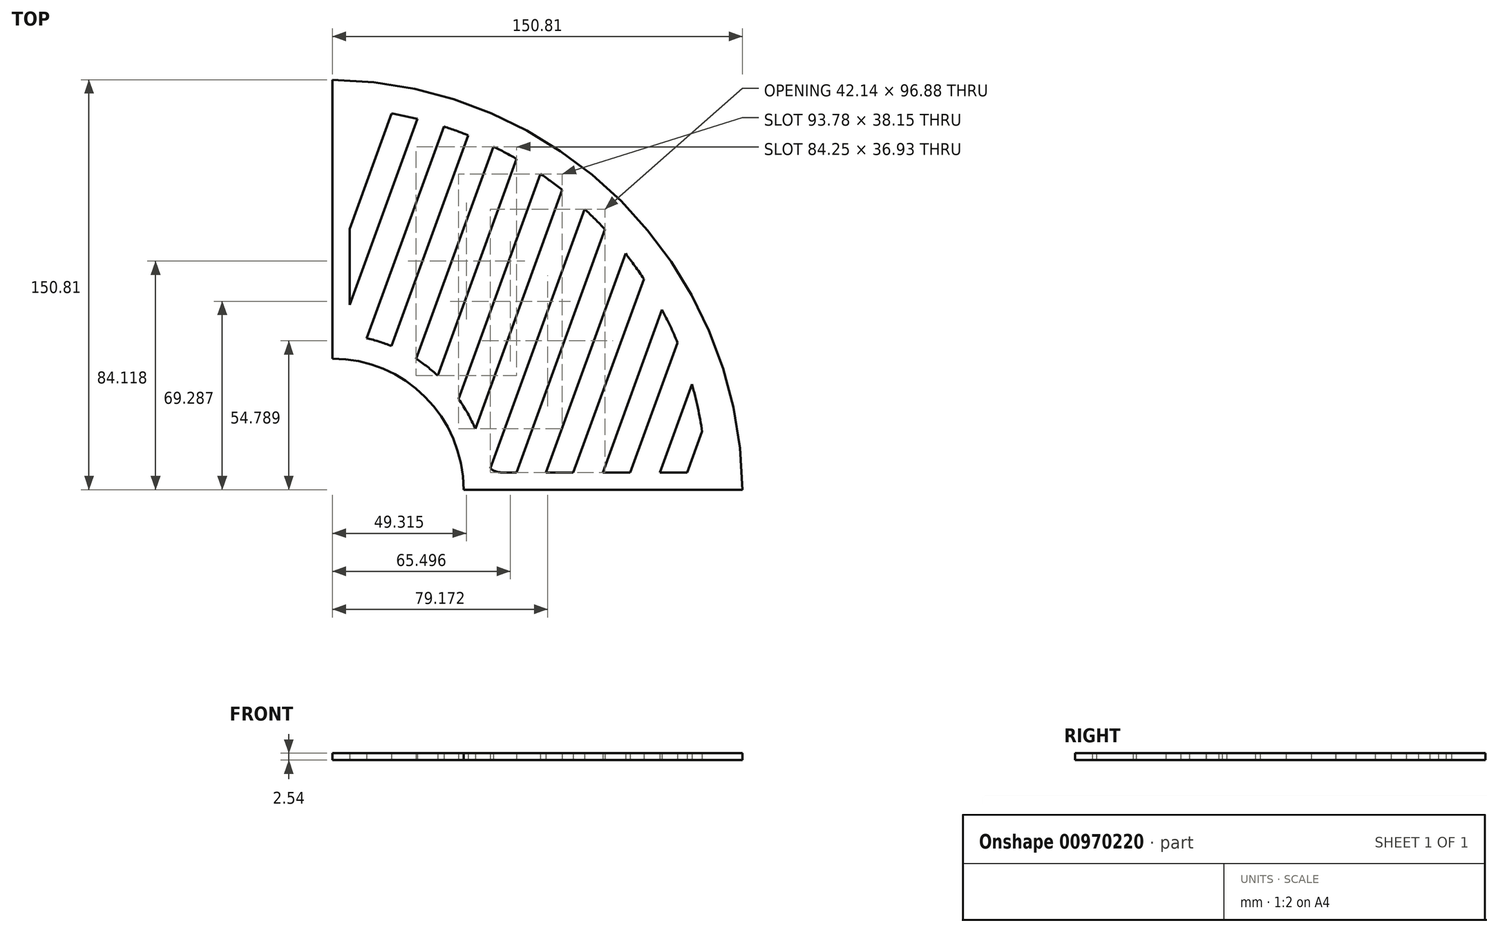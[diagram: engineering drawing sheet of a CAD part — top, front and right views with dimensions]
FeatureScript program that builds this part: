
annotation { "Feature Type Name" : "Feature", "Feature Type Description" : "" }
export const myFeature = defineFeature(function(context is Context, id is Id, definition is map)
    precondition{}
    {
        {
            var Q0;
            Q0=qCreatedBy(makeId("Top.planeOp"),FACE);
            var sketch = newSketch(context, id + "F0", { "sketchPlane" : qUnion([Q0])});
            skLineSegment(sketch, "E0", {"start": v(6.35, 68.05) * mm, "end": v(6.35, 95.9) * mm});
            skLineSegment(sketch, "E1", {"start": v(62.22, 6.35) * mm, "end": v(67.69, 6.35) * mm});
            skArc(sketch, "E2", {"start": v(52.58, 22.4) * mm, "mid": v(49.8, 28.03) * mm, "end": v(46.42, 33.33) * mm});
            skArc(sketch, "E3", {"start": v(136, 21.37) * mm, "mid": v(134.4, 30.18) * mm, "end": v(132.23, 38.87) * mm});
            skPoint(sketch, "E4.visualSharp", {"position": v(6.35, 140.23) * mm});
            skPoint(sketch, "E5.visualSharp", {"position": v(137.4, 6.35) * mm});
            skPoint(sketch, "E6.visualSharp", {"position": v(56.8, 6.35) * mm});
            skArc(sketch, "E6.filletArc", {"start": v(58.1, 7.86) * mm, "mid": v(60.02, 6.74) * mm, "end": v(62.22, 6.35) * mm});
            skPoint(sketch, "E7.visualSharp", {"position": v(6.35, 56.8) * mm});
            skPoint(sketch, "E8", {"position": v(6.35, 62.22) * mm});
            skLineSegment(sketch, "E9", {"start": v(0, 0) * mm, "end": v(150.81, 0) * mm});
            skLineSegment(sketch, "E10", {"start": v(0, 0) * mm, "end": v(0, 150.81) * mm});
            skArc(sketch, "E11", {"start": v(150.81, 0) * mm, "mid": v(106.18, 106.18) * mm, "end": v(0, 150.81) * mm});
            skLineSegment(sketch, "E12", {"start": v(0, 150.81) * mm, "end": v(0, 150.81) * mm});
            skLineSegment(sketch, "E13", {"start": v(150.81, 0) * mm, "end": v(150.81, 0) * mm});
            skArc(sketch, "E14", {"start": v(0, 48.26) * mm, "mid": v(34.12, 34.12) * mm, "end": v(48.26, 0) * mm});
            skLineSegment(sketch, "E15", {"start": v(12.68, 55.73) * mm, "end": v(41.04, 133.64) * mm});
            skLineSegment(sketch, "E16", {"start": v(21.76, 52.84) * mm, "end": v(49.99, 130.39) * mm});
            skArc(sketch, "E17.trimOffspring", {"start": v(31.24, 136.44) * mm, "mid": v(26.55, 137.5) * mm, "end": v(21.82, 138.42) * mm});
            skLineSegment(sketch, "E18.trimOffspring", {"start": v(6.35, 68.05) * mm, "end": v(31.24, 136.44) * mm});
            skLineSegment(sketch, "E19", {"start": v(6.35, 95.9) * mm, "end": v(21.82, 138.42) * mm});
            skPoint(sketch, "E19.endSnap0", {"position": v(22.27, 138.34) * mm});
            skLineSegment(sketch, "E20", {"start": v(30.85, 48.1) * mm, "end": v(59.3, 126.24) * mm});
            skLineSegment(sketch, "E21", {"start": v(38.76, 42) * mm, "end": v(67.78, 121.71) * mm});
            skLineSegment(sketch, "E22", {"start": v(46.42, 33.33) * mm, "end": v(76.58, 116.18) * mm});
            skArc(sketch, "E23.trimOffspring", {"start": v(21.76, 52.84) * mm, "mid": v(17.28, 54.47) * mm, "end": v(12.68, 55.73) * mm});
            skArc(sketch, "E24.trimOffspring", {"start": v(38.76, 42) * mm, "mid": v(34.94, 45.22) * mm, "end": v(30.85, 48.1) * mm});
            skArc(sketch, "E25.trimOffspring", {"start": v(67.78, 121.71) * mm, "mid": v(63.57, 124.05) * mm, "end": v(59.3, 126.24) * mm});
            skArc(sketch, "E26.trimOffspring", {"start": v(49.99, 130.39) * mm, "mid": v(45.54, 132.1) * mm, "end": v(41.04, 133.64) * mm});
            skPoint(sketch, "E27.orphan", {"position": v(22.27, 139.65) * mm});
            skLineSegment(sketch, "E28", {"start": v(84.57, 110.3) * mm, "end": v(52.58, 22.4) * mm});
            skArc(sketch, "E29.trimOffspring", {"start": v(84.57, 110.3) * mm, "mid": v(80.63, 113.3) * mm, "end": v(76.58, 116.18) * mm});
            skLineSegment(sketch, "E30.trimOffspring", {"start": v(58.1, 7.86) * mm, "end": v(92.81, 103.23) * mm});
            skLineSegment(sketch, "E31", {"start": v(67.69, 6.35) * mm, "end": v(100.24, 95.8) * mm});
            skLineSegment(sketch, "E32", {"start": v(78.5, 6.35) * mm, "end": v(107.82, 86.91) * mm});
            skLineSegment(sketch, "E33", {"start": v(88.63, 6.35) * mm, "end": v(114.55, 77.54) * mm});
            skLineSegment(sketch, "E34", {"start": v(99.45, 6.35) * mm, "end": v(121.24, 66.24) * mm});
            skLineSegment(sketch, "E35.trimOffspring", {"start": v(78.5, 6.35) * mm, "end": v(88.63, 6.35) * mm});
            skLineSegment(sketch, "E36.trimOffspring", {"start": v(99.45, 6.35) * mm, "end": v(109.58, 6.35) * mm});
            skArc(sketch, "E37.trimOffspring", {"start": v(114.55, 77.54) * mm, "mid": v(111.28, 82.3) * mm, "end": v(107.82, 86.91) * mm});
            skArc(sketch, "E38.trimOffspring", {"start": v(100.24, 95.8) * mm, "mid": v(96.6, 99.58) * mm, "end": v(92.81, 103.23) * mm});
            skLineSegment(sketch, "E39", {"start": v(109.58, 6.35) * mm, "end": v(126.96, 54.08) * mm});
            skLineSegment(sketch, "E40", {"start": v(120.4, 6.35) * mm, "end": v(132.23, 38.87) * mm});
            skLineSegment(sketch, "E41", {"start": v(130.53, 6.35) * mm, "end": v(136, 21.37) * mm});
            skLineSegment(sketch, "E42.trimOffspring", {"start": v(120.4, 6.35) * mm, "end": v(130.7, 6.35) * mm});
            skArc(sketch, "E43.trimOffspring", {"start": v(126.96, 54.08) * mm, "mid": v(124.25, 60.23) * mm, "end": v(121.24, 66.24) * mm});
            skPoint(sketch, "E44.trimOffspring.end.orphan", {"position": v(13.3, 139.65) * mm});
            skSolve(sketch);
        }
        {
            var Q0;
            Q0=makeQuery(id+"F0.imprint","IMPRINT",FACE,{"disambiguationData":[TD([[makeQuery(id+"F0.imprint","IMPRINT",EDGE,{"derivedFrom":sQuery(id+"F0.wireOp",EDGE,"E0")}),1.0]])]});
            extrude(context, id + "F1", {"entities" : qUnion([Q0]), "depth" : 2.54 * mm, "offsetDistance" : 25.4 * mm});
        }
    });
